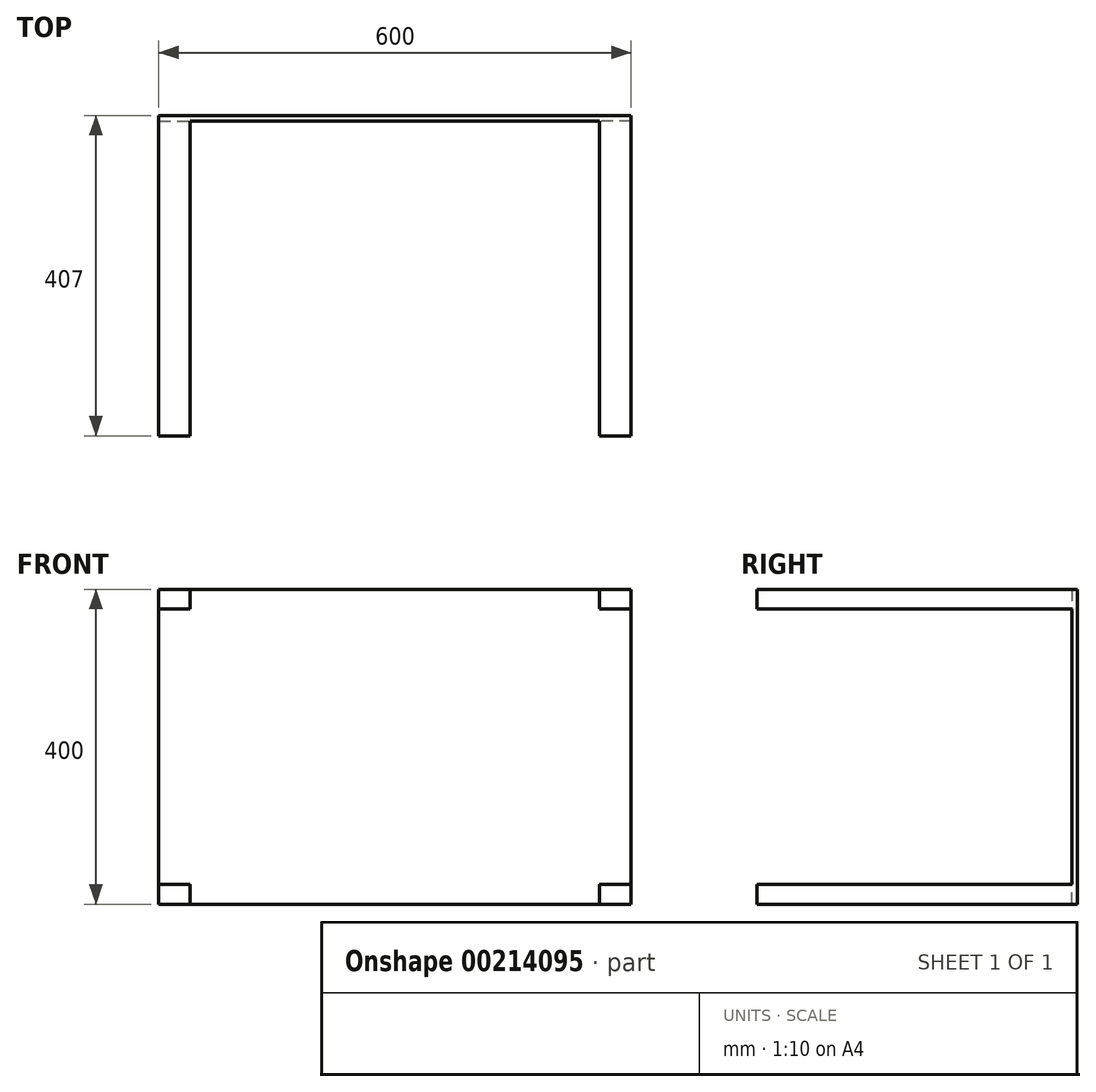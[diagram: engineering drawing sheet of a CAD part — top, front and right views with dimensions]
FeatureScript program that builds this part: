
annotation { "Feature Type Name" : "Feature", "Feature Type Description" : "" }
export const myFeature = defineFeature(function(context is Context, id is Id, definition is map)
    precondition{}
    {
        {
            var Q0;
            Q0=qCreatedBy(makeId("Front.planeOp"),FACE);
            var sketch = newSketch(context, id + "F0", { "sketchPlane" : qUnion([Q0])});
            skLineSegment(sketch, "E0.bottom", {"start": v(-206.87, 259.3) * mm, "end": v(393.13, 259.3) * mm});
            skLineSegment(sketch, "E0.top", {"start": v(-206.87, -140.7) * mm, "end": v(393.13, -140.7) * mm});
            skLineSegment(sketch, "E0.left", {"start": v(-206.87, 259.3) * mm, "end": v(-206.87, -140.7) * mm});
            skLineSegment(sketch, "E0.right", {"start": v(393.13, 259.3) * mm, "end": v(393.13, -140.7) * mm});
            skSolve(sketch);
        }
        {
            var Q0;
            Q0=makeQuery(id+"F0.imprint","IMPRINT",FACE,{"disambiguationData":[TD([[makeQuery(id+"F0.imprint","IMPRINT",EDGE,{"derivedFrom":sQuery(id+"F0.wireOp",EDGE,"E0.bottom")}),-1.0]])]});
            extrude(context, id + "F1", {"entities" : qUnion([Q0]), "depth" : 7 * mm});
        }
        {
            var Q0;
            Q0=makeQuery(id+"F1.opExtrude","CAP_FACE",FACE,{"disambiguationData":[OSD([sQuery(id+"F0.wireOp",EDGE,"E0.bottom"),sQuery(id+"F0.wireOp",EDGE,"E0.top"),sQuery(id+"F0.wireOp",EDGE,"E0.left"),sQuery(id+"F0.wireOp",EDGE,"E0.right")])],"isStart":false});
            var sketch = newSketch(context, id + "F2", { "sketchPlane" : qUnion([Q0])});
            skLineSegment(sketch, "E1.bottom", {"start": v(-206.87, 259.3) * mm, "end": v(-166.87, 259.3) * mm});
            skLineSegment(sketch, "E1.top", {"start": v(-206.87, 234.3) * mm, "end": v(-166.87, 234.3) * mm});
            skLineSegment(sketch, "E1.left", {"start": v(-206.87, 259.3) * mm, "end": v(-206.87, 234.3) * mm});
            skLineSegment(sketch, "E1.right", {"start": v(-166.87, 259.3) * mm, "end": v(-166.87, 234.3) * mm});
            skLineSegment(sketch, "E2.bottom", {"start": v(-206.87, -140.7) * mm, "end": v(-166.87, -140.7) * mm});
            skLineSegment(sketch, "E2.top", {"start": v(-206.87, -115.7) * mm, "end": v(-166.87, -115.7) * mm});
            skLineSegment(sketch, "E2.left", {"start": v(-206.87, -140.7) * mm, "end": v(-206.87, -115.7) * mm});
            skLineSegment(sketch, "E2.right", {"start": v(-166.87, -140.7) * mm, "end": v(-166.87, -115.7) * mm});
            skLineSegment(sketch, "E3.bottom", {"start": v(393.13, 259.3) * mm, "end": v(353.13, 259.3) * mm});
            skLineSegment(sketch, "E3.top", {"start": v(393.13, 234.3) * mm, "end": v(353.13, 234.3) * mm});
            skLineSegment(sketch, "E3.left", {"start": v(393.13, 259.3) * mm, "end": v(393.13, 234.3) * mm});
            skLineSegment(sketch, "E3.right", {"start": v(353.13, 259.3) * mm, "end": v(353.13, 234.3) * mm});
            skLineSegment(sketch, "E4.bottom", {"start": v(393.13, -140.7) * mm, "end": v(353.13, -140.7) * mm});
            skLineSegment(sketch, "E4.top", {"start": v(393.13, -115.7) * mm, "end": v(353.13, -115.7) * mm});
            skLineSegment(sketch, "E4.left", {"start": v(393.13, -140.7) * mm, "end": v(393.13, -115.7) * mm});
            skLineSegment(sketch, "E4.right", {"start": v(353.13, -140.7) * mm, "end": v(353.13, -115.7) * mm});
            skSolve(sketch);
        }
        {
            var Q0;
            Q0=makeQuery(id+"F2.imprint","IMPRINT",FACE,{"disambiguationData":[TD([[makeQuery(id+"F2.imprint","IMPRINT",EDGE,{"derivedFrom":sQuery(id+"F2.wireOp",EDGE,"E1.bottom")}),-1.0]])]});
            extrude(context, id + "F3", {"entities" : qUnion([Q0]), "operationType" : NewBodyOperationType.ADD, "depth" : 400 * mm});
        }
        {
            var Q0;
            Q0=makeQuery(id+"F2.imprint","IMPRINT",FACE,{"disambiguationData":[TD([[makeQuery(id+"F2.imprint","IMPRINT",EDGE,{"derivedFrom":sQuery(id+"F2.wireOp",EDGE,"E2.bottom")}),1.0]])]});
            extrude(context, id + "F4", {"entities" : qUnion([Q0]), "operationType" : NewBodyOperationType.ADD, "depth" : 400 * mm});
        }
        {
            var Q0;
            Q0=makeQuery(id+"F2.imprint","IMPRINT",FACE,{"disambiguationData":[TD([[makeQuery(id+"F2.imprint","IMPRINT",EDGE,{"derivedFrom":sQuery(id+"F2.wireOp",EDGE,"E3.bottom")}),-1.0]])]});
            extrude(context, id + "F5", {"entities" : qUnion([Q0]), "operationType" : NewBodyOperationType.ADD, "depth" : 400 * mm});
        }
        {
            var Q0;
            Q0=makeQuery(id+"F2.imprint","IMPRINT",FACE,{"disambiguationData":[TD([[makeQuery(id+"F2.imprint","IMPRINT",EDGE,{"derivedFrom":sQuery(id+"F2.wireOp",EDGE,"E4.bottom")}),1.0]])]});
            extrude(context, id + "F6", {"entities" : qUnion([Q0]), "operationType" : NewBodyOperationType.ADD, "depth" : 400 * mm});
        }
    });
